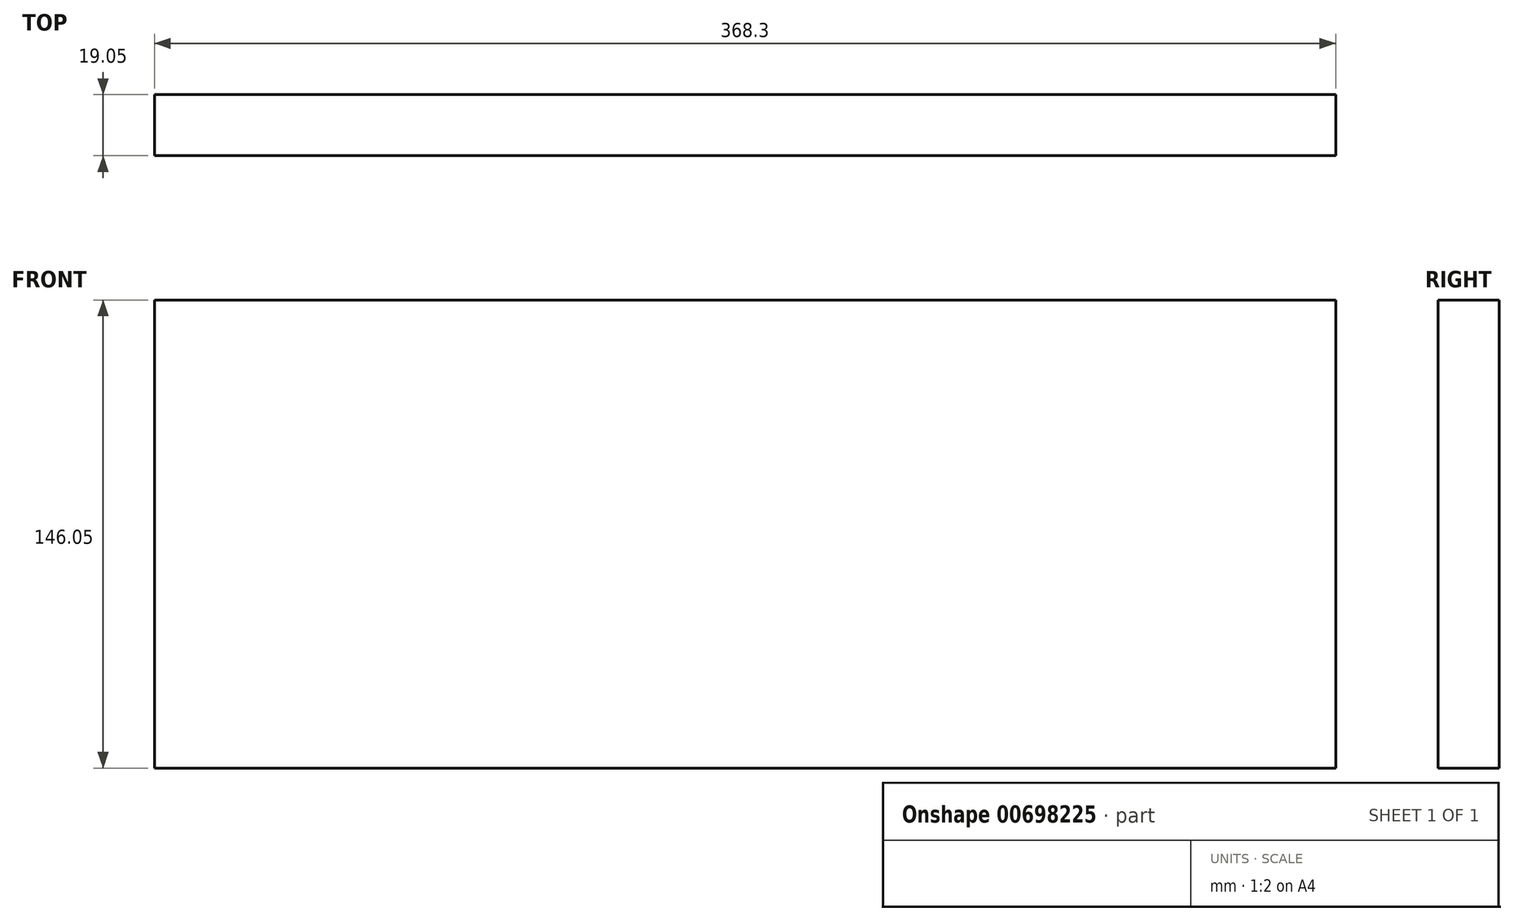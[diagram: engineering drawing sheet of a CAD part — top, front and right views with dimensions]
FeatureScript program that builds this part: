
annotation { "Feature Type Name" : "Feature", "Feature Type Description" : "" }
export const myFeature = defineFeature(function(context is Context, id is Id, definition is map)
    precondition{}
    {
        {
            var Q0;
            Q0=qCreatedBy(makeId("Front.planeOp"),FACE);
            var sketch = newSketch(context, id + "F0", { "sketchPlane" : qUnion([Q0])});
            skLineSegment(sketch, "E0.bottom", {"start": v(-285.72, 77.87) * mm, "end": v(82.58, 77.87) * mm});
            skLineSegment(sketch, "E0.top", {"start": v(-285.72, -68.18) * mm, "end": v(82.58, -68.18) * mm});
            skLineSegment(sketch, "E0.left", {"start": v(-285.72, 77.87) * mm, "end": v(-285.72, -68.18) * mm});
            skLineSegment(sketch, "E0.right", {"start": v(82.58, 77.87) * mm, "end": v(82.58, -68.18) * mm});
            skSolve(sketch);
        }
        {
            var Q0;
            Q0=makeQuery(id+"F0.imprint","IMPRINT",FACE,{"disambiguationData":[TD([[makeQuery(id+"F0.imprint","IMPRINT",EDGE,{"derivedFrom":sQuery(id+"F0.wireOp",EDGE,"E0.bottom")}),-1.0]])]});
            extrude(context, id + "F1", {"entities" : qUnion([Q0]), "depth" : 19.05 * mm, "offsetDistance" : 25.4 * mm});
        }
    });
